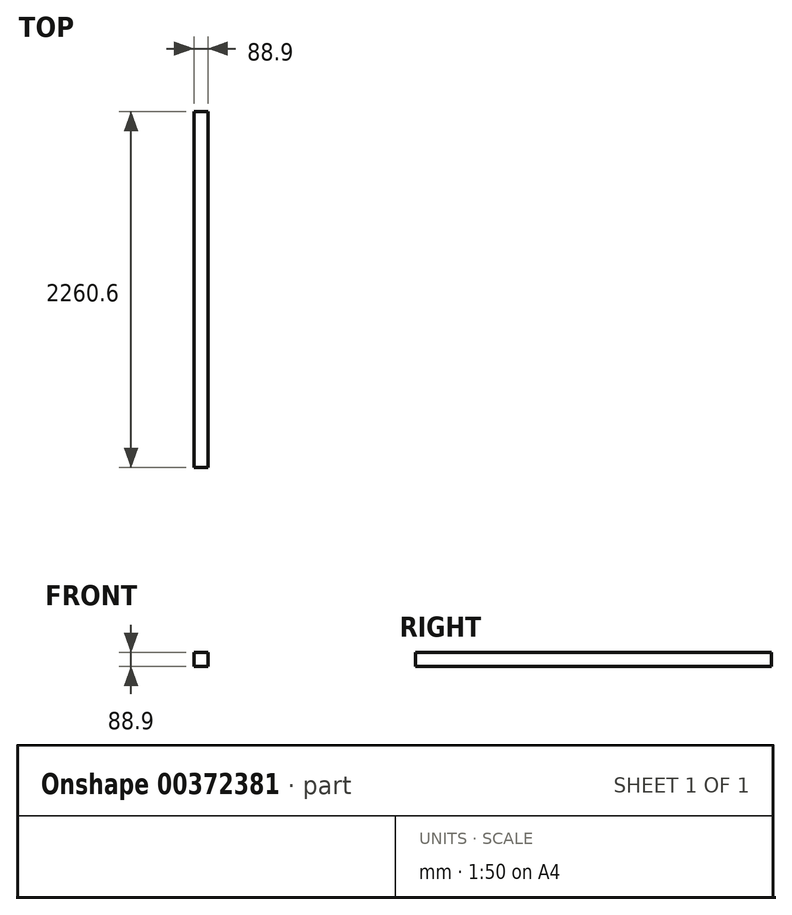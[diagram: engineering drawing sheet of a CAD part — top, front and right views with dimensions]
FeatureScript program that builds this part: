
annotation { "Feature Type Name" : "Feature", "Feature Type Description" : "" }
export const myFeature = defineFeature(function(context is Context, id is Id, definition is map)
    precondition{}
    {
        {
            var Q0;
            Q0=qCreatedBy(makeId("Front.planeOp"),FACE);
            var sketch = newSketch(context, id + "F0", { "sketchPlane" : qUnion([Q0])});
            skLineSegment(sketch, "E0.bottom", {"start": v(-44.45, 44.45) * mm, "end": v(44.45, 44.45) * mm});
            skLineSegment(sketch, "E0.top", {"start": v(-44.45, -44.45) * mm, "end": v(44.45, -44.45) * mm});
            skLineSegment(sketch, "E0.left", {"start": v(-44.45, 44.45) * mm, "end": v(-44.45, -44.45) * mm});
            skLineSegment(sketch, "E0.right", {"start": v(44.45, 44.45) * mm, "end": v(44.45, -44.45) * mm});
            skPoint(sketch, "E0.middle", {"position": v(0, 0) * mm});
            skSolve(sketch);
        }
        {
            var Q0;
            Q0=qSketchRegion(id+"F0",true);
            extrude(context, id + "F1", {"entities" : qUnion([Q0]), "endBound" : BoundingType.SYMMETRIC, "oppositeDirection" : true, "depth" : 2260.6 * mm});
        }
    });
